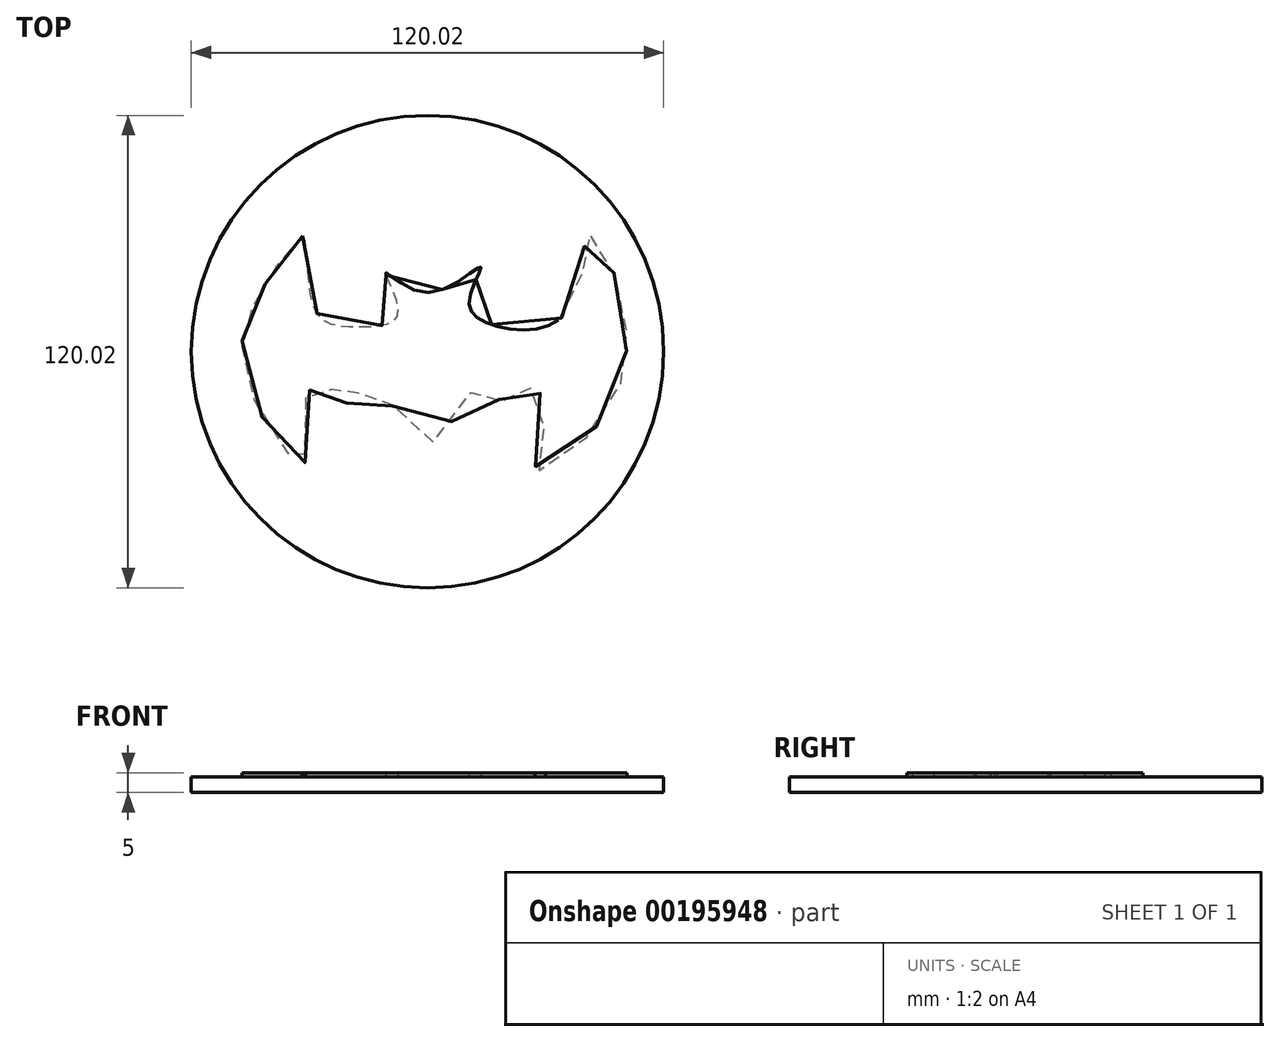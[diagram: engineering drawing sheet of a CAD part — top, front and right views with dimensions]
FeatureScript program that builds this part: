
annotation { "Feature Type Name" : "Feature", "Feature Type Description" : "" }
export const myFeature = defineFeature(function(context is Context, id is Id, definition is map)
    precondition{}
    {
        {
            var Q0;
            Q0=qCreatedBy(makeId("Top.planeOp"),FACE);
            var sketch = newSketch(context, id + "F0", { "sketchPlane" : qUnion([Q0])});
            skCircle(sketch, "E0", {"center": v(0, 0) * mm, "radius": 60.01 * mm});
            skSolve(sketch);
        }
        {
            var Q0;
            Q0 = qSketchRegion(id + "F0", true);
            extrude(context, id + "F1", {"entities" : qUnion([Q0]), "depth" : 4 * mm});
        }
        {
            var Q0;
            Q0=makeQuery(id+"F1.opExtrude","CAP_FACE",FACE,{"disambiguationData":[OSD([sQuery(id+"F0.wireOp",EDGE,"E0")])],"isStart":false});
            var sketch = newSketch(context, id + "F2", { "sketchPlane" : qUnion([Q0])});
            skFitSpline(sketch, "E1", {"points": [v(-31.75, 29.36) * mm, v(-37.8, 22.62) * mm, v(-44.7, 10.87) * mm, v(-47.12, 0) * mm, v(-40.38, -19.36) * mm, v(-31.4, -28.7) * mm, v(-31.75, -15.74) * mm, v(-26.39, -7.44) * mm, v(-20.86, -13.14) * mm, v(-14.47, -7.96) * mm, v(0, -23.34) * mm, v(12.83, -9) * mm, v(19.22, -12.63) * mm, v(24.75, -9.34) * mm, v(29.94, -13.66) * mm, v(27.69, -29.9) * mm, v(43.76, -17.98) * mm, v(50.5, 0) * mm, v(48.08, 18.13) * mm, v(41, 29.7) * mm, v(38.57, 16.57) * mm, v(29.6, 6.2) * mm, v(14.04, 7.76) * mm, v(10.58, 13.46) * mm, v(13.52, 21.58) * mm, v(0, 15.02) * mm, v(-10.67, 20.03) * mm, v(-7.56, 9.66) * mm, v(-17.58, 6.2) * mm, v(-28.64, 10.7) * mm, v(-31.75, 29.36) * mm]});
            skSolve(sketch);
        }
        {
            var Q0;
            Q0=makeQuery(id+"F2.imprint","IMPRINT",FACE,{"disambiguationData":[TD([[makeQuery(id+"F2.imprint","IMPRINT",EDGE,{"derivedFrom":sQuery(id+"F2.wireOp",EDGE,"E1")}),1.0]])]});
            extrude(context, id + "F3", {"entities" : qUnion([Q0]), "operationType" : NewBodyOperationType.ADD, "depth" : 1 * mm});
        }
    });
